# Revit family: KEUCO_59541000170_
name_source: partatom
category: Generic Models
revit_build: Autodesk Revit 2016 (Build: 20150220_1215(x64)
units: mm (PartAtom-declared; Revit-internal decimal feet)

## family parameters
Always vertical = No
Can host rebar = No
Cut with Voids When Loaded = No
Part Type = Normal
Room Calculation Point = No
Round Connector Dimension = Use Diameter
Shared = No
Work Plane-Based = Yes

## types (1)
- 59541000170
    Artikelnummer = 59541000170
    Ausschreibungstext = KEUCO IXMO UP Funktionseinheit für Absperrventil 
mit Schlauchanschluss DN15, 59541000170
schallentkoppelter Grundkörper aus entzinkungsarmen Messing
für den Wandeinbau, frei positionierbar,
Einbautiefe von 80 mm – 110 mm, 
Grundplatte mit Einstellschrauben zur optimalen Ausrichtung,
Anschlüsse G 1/2 Zoll, mit farblicher Kennzeichnung,
Hinweis: passend zu Artikel-Nr. 
59541010101, 59541010102, 59541010201,
59541010202, 59541011101, 59541011102,
59541011201, 59541011202,
    Breite = 45 mm  [stored 0.147638 ft]
    Default Elevation = 1219 mm
    Description = Grundkörper für Wandeinbau,
Einbautiefe 80 - 110 mm
    Gewicht = 0
    Kategorie = ARM
    Manufacturer = KEUCO
    Material = Stahl, verchromt
    Serie = Plan
    URL = https://www.keuco.com
    Verwendung = DU / ZU

note: [stored X ft] marks values corroborated as IEEE doubles in the binary element streams (Revit-internal decimal feet)

## geometry (parser evidence)
native form markers: Sweep x3
no freeform markers — native parametric forms only
